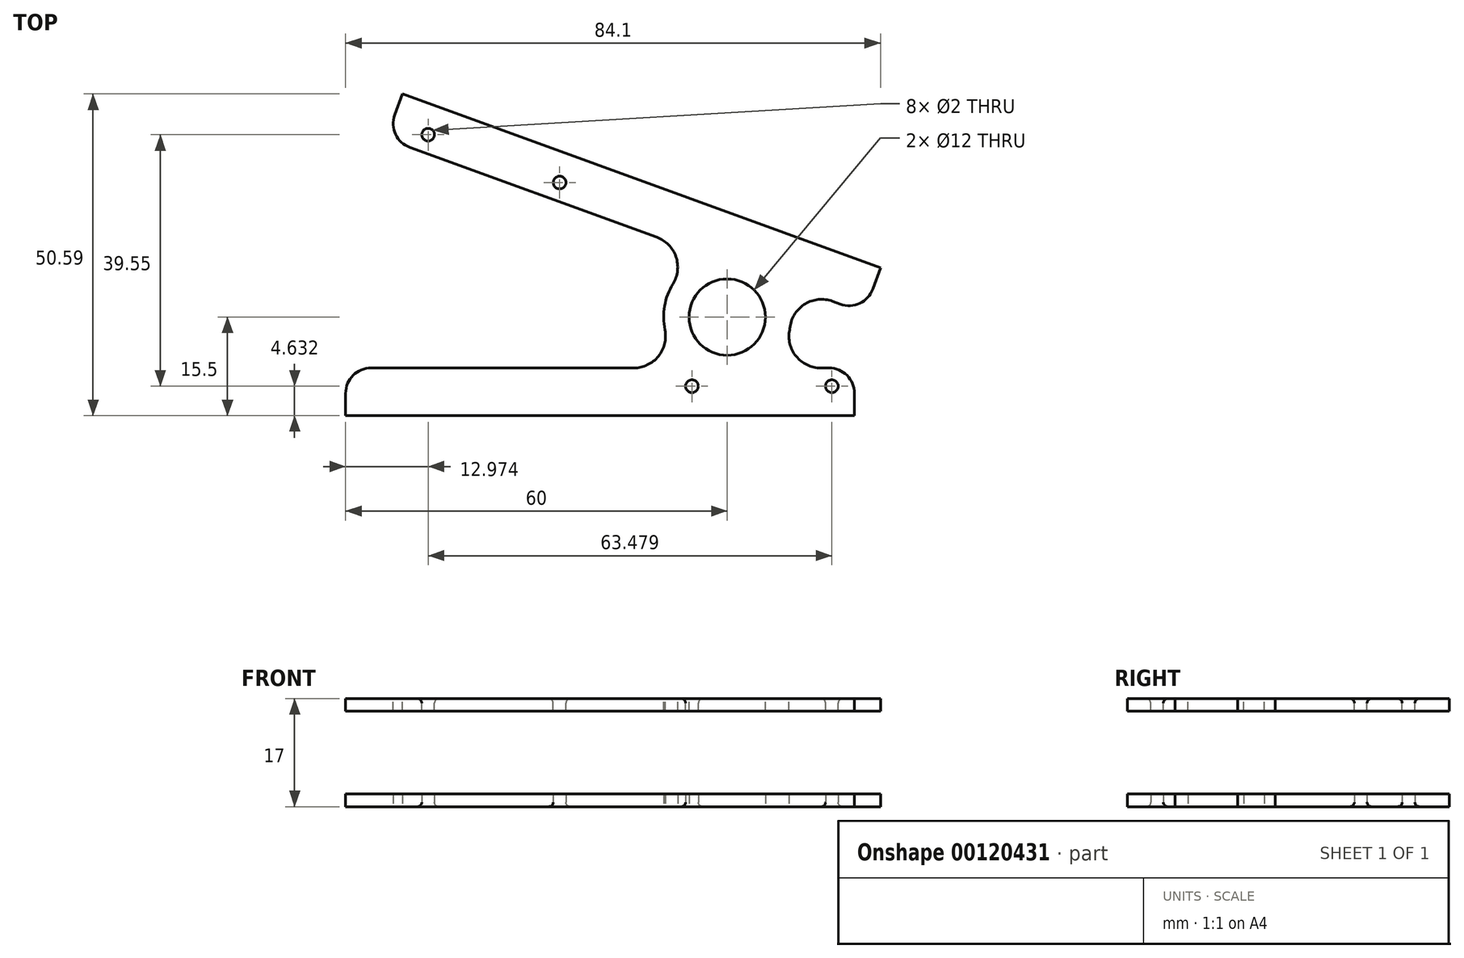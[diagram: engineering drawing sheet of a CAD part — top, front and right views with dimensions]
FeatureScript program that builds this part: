
annotation { "Feature Type Name" : "Feature", "Feature Type Description" : "" }
export const myFeature = defineFeature(function(context is Context, id is Id, definition is map)
    precondition{}
    {
        {
            var Q0;
            Q0=qCreatedBy(makeId("Top.planeOp"),FACE);
            var sketch = newSketch(context, id + "F0", { "sketchPlane" : qUnion([Q0])});
            skLineSegment(sketch, "E0.bottom", {"start": v(-60, -15.5) * mm, "end": v(20, -15.5) * mm});
            skLineSegment(sketch, "E0.top", {"start": v(-56, -8) * mm, "end": v(-14.7, -8) * mm});
            skLineSegment(sketch, "E0.left", {"start": v(-60, -15.5) * mm, "end": v(-60, -12) * mm});
            skLineSegment(sketch, "E0.right", {"start": v(20, -15.5) * mm, "end": v(20, -12) * mm});
            skPoint(sketch, "E0.middle", {"position": v(-20, -11.75) * mm});
            skCircle(sketch, "E1", {"center": v(-54, -10.87) * mm, "radius": 1 * mm});
            skCircle(sketch, "E2", {"center": v(-32, -10.87) * mm, "radius": 1 * mm});
            skCircle(sketch, "E3.MirrorC", {"center": v(16.45, -10.87) * mm, "radius": 1 * mm});
            skCircle(sketch, "E4.MirrorC", {"center": v(-5.55, -10.87) * mm, "radius": 1 * mm});
            skCircle(sketch, "E5", {"center": v(0, 0) * mm, "radius": 6 * mm});
            skArc(sketch, "E6.0", {"start": v(9.8, -2) * mm, "mid": v(9.85, -1.74) * mm, "end": v(9.9, -1.47) * mm});
            skLineSegment(sketch, "E7.trimOffspring", {"start": v(14.7, -8) * mm, "end": v(16, -8) * mm});
            skPoint(sketch, "E8.visualSharp", {"position": v(-6, -8) * mm});
            skArc(sketch, "E8.filletArc", {"start": v(-14.7, -8) * mm, "mid": v(-10.82, -6.16) * mm, "end": v(-9.8, -2) * mm});
            skPoint(sketch, "E9.visualSharp", {"position": v(6, -8) * mm});
            skArc(sketch, "E9.filletArc", {"start": v(9.8, -2) * mm, "mid": v(10.82, -6.16) * mm, "end": v(14.7, -8) * mm});
            skPoint(sketch, "E10.visualSharp", {"position": v(20, -8) * mm});
            skArc(sketch, "E10.filletArc", {"start": v(20, -12) * mm, "mid": v(18.83, -9.17) * mm, "end": v(16, -8) * mm});
            skPoint(sketch, "E11.visualSharp", {"position": v(-60, -8) * mm});
            skArc(sketch, "E11.filletArc", {"start": v(-56, -8) * mm, "mid": v(-58.83, -9.17) * mm, "end": v(-60, -12) * mm});
            skLineSegment(sketch, "E12.MirrorCS", {"start": v(-51.08, 35.09) * mm, "end": v(24.1, 7.72) * mm});
            skLineSegment(sketch, "E13.MirrorCS", {"start": v(-49.89, 26.67) * mm, "end": v(-11.07, 12.54) * mm});
            skArc(sketch, "E14.MirrorCS", {"start": v(-49.89, 26.67) * mm, "mid": v(-52.14, 28.74) * mm, "end": v(-52.28, 31.8) * mm});
            skLineSegment(sketch, "E15.MirrorCS", {"start": v(-51.08, 35.09) * mm, "end": v(-52.28, 31.8) * mm});
            skArc(sketch, "E16.MirrorCS", {"start": v(-11.07, 12.54) * mm, "mid": v(-8.06, 9.5) * mm, "end": v(-8.52, 5.23) * mm});
            skLineSegment(sketch, "E17.MirrorCS", {"start": v(24.1, 7.72) * mm, "end": v(22.9, 4.44) * mm});
            skArc(sketch, "E18.MirrorCS", {"start": v(22.9, 4.44) * mm, "mid": v(20.83, 2.18) * mm, "end": v(17.77, 2.05) * mm});
            skLineSegment(sketch, "E19.MirrorCS", {"start": v(16.55, 2.5) * mm, "end": v(17.77, 2.05) * mm});
            skArc(sketch, "E20.MirrorCS", {"start": v(9.9, -1.47) * mm, "mid": v(12.28, 2.09) * mm, "end": v(16.55, 2.5) * mm});
            skArc(sketch, "E21.trimOffspring", {"start": v(-8.52, 5.23) * mm, "mid": v(-9.85, 1.74) * mm, "end": v(-9.8, -2) * mm});
            skCircle(sketch, "E22.MirrorC", {"center": v(-47.03, 28.68) * mm, "radius": 1 * mm});
            skCircle(sketch, "E23.MirrorC", {"center": v(-26.35, 21.16) * mm, "radius": 1 * mm});
            skCircle(sketch, "E24.MirrorC", {"center": v(-1.5, 12.11) * mm, "radius": 1 * mm});
            skCircle(sketch, "E25.MirrorC", {"center": v(19.18, 4.59) * mm, "radius": 1 * mm});
            skSolve(sketch);
        }
        {
            var Q0;
            Q0=makeQuery(id+"F0.imprint","IMPRINT",FACE,{"disambiguationData":[TD([[makeQuery(id+"F0.imprint","IMPRINT",EDGE,{"derivedFrom":sQuery(id+"F0.wireOp",EDGE,"E0.bottom")}),1.0]])]});
            var Q1;
            Q1=makeQuery(id+"F0.imprint","IMPRINT",FACE,{"disambiguationData":[TD([[makeQuery(id+"F0.imprint","IMPRINT",EDGE,{"derivedFrom":sQuery(id+"F0.wireOp",EDGE,"E1")}),1.0]])]});
            var Q2;
            Q2=makeQuery(id+"F0.imprint","IMPRINT",FACE,{"disambiguationData":[TD([[makeQuery(id+"F0.imprint","IMPRINT",EDGE,{"derivedFrom":sQuery(id+"F0.wireOp",EDGE,"E2")}),1.0]])]});
            var Q3;
            Q3=makeQuery(id+"F0.imprint","IMPRINT",FACE,{"disambiguationData":[TD([[makeQuery(id+"F0.imprint","IMPRINT",EDGE,{"derivedFrom":sQuery(id+"F0.wireOp",EDGE,"E4.MirrorC")}),-1.0]])]});
            var Q4;
            Q4=makeQuery(id+"F0.imprint","IMPRINT",FACE,{"disambiguationData":[TD([[makeQuery(id+"F0.imprint","IMPRINT",EDGE,{"derivedFrom":sQuery(id+"F0.wireOp",EDGE,"E3.MirrorC")}),-1.0]])]});
            var Q5;
            Q5=makeQuery(id+"F0.imprint","IMPRINT",FACE,{"disambiguationData":[TD([[makeQuery(id+"F0.imprint","IMPRINT",EDGE,{"derivedFrom":sQuery(id+"F0.wireOp",EDGE,"E22.MirrorC")}),-1.0]])]});
            var Q6;
            Q6=makeQuery(id+"F0.imprint","IMPRINT",FACE,{"disambiguationData":[TD([[makeQuery(id+"F0.imprint","IMPRINT",EDGE,{"derivedFrom":sQuery(id+"F0.wireOp",EDGE,"E23.MirrorC")}),-1.0]])]});
            var Q7;
            Q7=makeQuery(id+"F0.imprint","IMPRINT",FACE,{"disambiguationData":[TD([[makeQuery(id+"F0.imprint","IMPRINT",EDGE,{"derivedFrom":sQuery(id+"F0.wireOp",EDGE,"E24.MirrorC")}),1.0]])]});
            var Q8;
            Q8=makeQuery(id+"F0.imprint","IMPRINT",FACE,{"disambiguationData":[TD([[makeQuery(id+"F0.imprint","IMPRINT",EDGE,{"derivedFrom":sQuery(id+"F0.wireOp",EDGE,"E25.MirrorC")}),1.0]])]});
            extrude(context, id + "F1", {"entities" : qUnion([Q0, Q1, Q2, Q3, Q4, Q5, Q6, Q7, Q8]), "oppositeDirection" : true, "depth" : 1 * mm});
        }
        {
            var Q0;
            Q0=makeQuery(id+"F0.imprint","IMPRINT",FACE,{"disambiguationData":[TD([[makeQuery(id+"F0.imprint","IMPRINT",EDGE,{"derivedFrom":sQuery(id+"F0.wireOp",EDGE,"E22.MirrorC")}),-1.0]])]});
            var Q1;
            Q1=makeQuery(id+"F0.imprint","IMPRINT",FACE,{"disambiguationData":[TD([[makeQuery(id+"F0.imprint","IMPRINT",EDGE,{"derivedFrom":sQuery(id+"F0.wireOp",EDGE,"E23.MirrorC")}),-1.0]])]});
            var Q2;
            Q2=makeQuery(id+"F0.imprint","IMPRINT",FACE,{"disambiguationData":[TD([[makeQuery(id+"F0.imprint","IMPRINT",EDGE,{"derivedFrom":sQuery(id+"F0.wireOp",EDGE,"E24.MirrorC")}),1.0]])]});
            var Q3;
            Q3=makeQuery(id+"F0.imprint","IMPRINT",FACE,{"disambiguationData":[TD([[makeQuery(id+"F0.imprint","IMPRINT",EDGE,{"derivedFrom":sQuery(id+"F0.wireOp",EDGE,"E25.MirrorC")}),1.0]])]});
            var Q4;
            Q4=makeQuery(id+"F0.imprint","IMPRINT",FACE,{"disambiguationData":[TD([[makeQuery(id+"F0.imprint","IMPRINT",EDGE,{"derivedFrom":sQuery(id+"F0.wireOp",EDGE,"E3.MirrorC")}),-1.0]])]});
            var Q5;
            Q5=makeQuery(id+"F0.imprint","IMPRINT",FACE,{"disambiguationData":[TD([[makeQuery(id+"F0.imprint","IMPRINT",EDGE,{"derivedFrom":sQuery(id+"F0.wireOp",EDGE,"E4.MirrorC")}),-1.0]])]});
            var Q6;
            Q6=makeQuery(id+"F0.imprint","IMPRINT",FACE,{"disambiguationData":[TD([[makeQuery(id+"F0.imprint","IMPRINT",EDGE,{"derivedFrom":sQuery(id+"F0.wireOp",EDGE,"E2")}),1.0]])]});
            var Q7;
            Q7=makeQuery(id+"F0.imprint","IMPRINT",FACE,{"disambiguationData":[TD([[makeQuery(id+"F0.imprint","IMPRINT",EDGE,{"derivedFrom":sQuery(id+"F0.wireOp",EDGE,"E1")}),1.0]])]});
            extrude(context, id + "F2", {"entities" : qUnion([Q0, Q1, Q2, Q3, Q4, Q5, Q6, Q7]), "operationType" : NewBodyOperationType.ADD, "depth" : 1 * mm});
        }
        {
            var Q0;
            Q0=makeQuery(id+"F2.opExtrude","CAP_EDGE",EDGE,{"disambiguationData":[OSD([sQuery(id+"F0.wireOp",EDGE,"E22.MirrorC")])],"isStart":false});
            var Q1;
            Q1=makeQuery(id+"F2.opExtrude","CAP_EDGE",EDGE,{"disambiguationData":[OSD([sQuery(id+"F0.wireOp",EDGE,"E23.MirrorC")])],"isStart":false});
            var Q2;
            Q2=makeQuery(id+"F2.opExtrude","CAP_EDGE",EDGE,{"disambiguationData":[OSD([sQuery(id+"F0.wireOp",EDGE,"E24.MirrorC")])],"isStart":false});
            var Q3;
            Q3=makeQuery(id+"F2.opExtrude","CAP_EDGE",EDGE,{"disambiguationData":[OSD([sQuery(id+"F0.wireOp",EDGE,"E25.MirrorC")])],"isStart":false});
            var Q4;
            Q4=makeQuery(id+"F2.opExtrude","CAP_EDGE",EDGE,{"disambiguationData":[OSD([sQuery(id+"F0.wireOp",EDGE,"E1")])],"isStart":false});
            var Q5;
            Q5=makeQuery(id+"F2.opExtrude","CAP_EDGE",EDGE,{"disambiguationData":[OSD([sQuery(id+"F0.wireOp",EDGE,"E2")])],"isStart":false});
            var Q6;
            Q6=makeQuery(id+"F2.opExtrude","CAP_EDGE",EDGE,{"disambiguationData":[OSD([sQuery(id+"F0.wireOp",EDGE,"E4.MirrorC")])],"isStart":false});
            var Q7;
            Q7=makeQuery(id+"F2.opExtrude","CAP_EDGE",EDGE,{"disambiguationData":[OSD([sQuery(id+"F0.wireOp",EDGE,"E3.MirrorC")])],"isStart":false});
            fillet(context, id + "F3", {"entities" : qUnion([Q0, Q1, Q2, Q3, Q4, Q5, Q6, Q7]), "radius" : 0.7 * mm, "allowEdgeOverflow" : false});
        }
        {
            var Q0;
            Q0=makeQuery(id+"F1.opExtrude","SWEPT_BODY",BODY,{"disambiguationData":[OSD([sQuery(id+"F0.wireOp",EDGE,"E0.bottom"),sQuery(id+"F0.wireOp",EDGE,"E0.top"),sQuery(id+"F0.wireOp",EDGE,"E0.left"),sQuery(id+"F0.wireOp",EDGE,"E0.right"),sQuery(id+"F0.wireOp",EDGE,"E5"),sQuery(id+"F0.wireOp",EDGE,"E6.0"),sQuery(id+"F0.wireOp",EDGE,"E7.trimOffspring"),sQuery(id+"F0.wireOp",EDGE,"E8.filletArc"),sQuery(id+"F0.wireOp",EDGE,"E9.filletArc"),sQuery(id+"F0.wireOp",EDGE,"E10.filletArc"),sQuery(id+"F0.wireOp",EDGE,"E11.filletArc"),sQuery(id+"F0.wireOp",EDGE,"E12.MirrorCS"),sQuery(id+"F0.wireOp",EDGE,"E13.MirrorCS"),sQuery(id+"F0.wireOp",EDGE,"E14.MirrorCS"),sQuery(id+"F0.wireOp",EDGE,"E15.MirrorCS"),sQuery(id+"F0.wireOp",EDGE,"E16.MirrorCS"),sQuery(id+"F0.wireOp",EDGE,"E17.MirrorCS"),sQuery(id+"F0.wireOp",EDGE,"E18.MirrorCS"),sQuery(id+"F0.wireOp",EDGE,"E19.MirrorCS"),sQuery(id+"F0.wireOp",EDGE,"E20.MirrorCS"),sQuery(id+"F0.wireOp",EDGE,"E21.trimOffspring")])]});
            var Q1;
            Q1=qCreatedBy(makeId("Top.planeOp"),FACE);
            mirror(context, id + "F4", {"entities" : qUnion([Q0]), "mirrorPlane" : qUnion([Q1])});
        }
        {
            var Q0;
            Q0=makeQuery(id+"F4.opPattern","COPY",BODY,{"derivedFrom":makeQuery(id+"F1.opExtrude","SWEPT_BODY",BODY,{"disambiguationData":[OSD([sQuery(id+"F0.wireOp",EDGE,"E0.bottom"),sQuery(id+"F0.wireOp",EDGE,"E0.top"),sQuery(id+"F0.wireOp",EDGE,"E0.left"),sQuery(id+"F0.wireOp",EDGE,"E0.right"),sQuery(id+"F0.wireOp",EDGE,"E5"),sQuery(id+"F0.wireOp",EDGE,"E6.0"),sQuery(id+"F0.wireOp",EDGE,"E7.trimOffspring"),sQuery(id+"F0.wireOp",EDGE,"E8.filletArc"),sQuery(id+"F0.wireOp",EDGE,"E9.filletArc"),sQuery(id+"F0.wireOp",EDGE,"E10.filletArc"),sQuery(id+"F0.wireOp",EDGE,"E11.filletArc"),sQuery(id+"F0.wireOp",EDGE,"E12.MirrorCS"),sQuery(id+"F0.wireOp",EDGE,"E13.MirrorCS"),sQuery(id+"F0.wireOp",EDGE,"E14.MirrorCS"),sQuery(id+"F0.wireOp",EDGE,"E15.MirrorCS"),sQuery(id+"F0.wireOp",EDGE,"E16.MirrorCS"),sQuery(id+"F0.wireOp",EDGE,"E17.MirrorCS"),sQuery(id+"F0.wireOp",EDGE,"E18.MirrorCS"),sQuery(id+"F0.wireOp",EDGE,"E19.MirrorCS"),sQuery(id+"F0.wireOp",EDGE,"E20.MirrorCS"),sQuery(id+"F0.wireOp",EDGE,"E21.trimOffspring")])]}),"instanceName":"1"});
            transform(context, id + "F5", {"entities" : qUnion([Q0]), "transformType" : TransformType.TRANSLATION_3D, "dx" : 0 * mm, "dy" : 0 * mm, "dz" : -15 * mm, "makeCopy" : false});
        }
    });
